# Revit family: Indirect-Water-Heater_AO_Smith-IT-500_G_B
name_source: partatom
category: Mechanical Equipment
revit_build: Autodesk Revit 2016 (Build: 20170117_1200(x64)
units: mm (PartAtom-declared; Revit-internal decimal feet)

## family parameters
Always vertical = Yes
Cut with Voids When Loaded = No
OmniClass Number = 23.75.00.00
OmniClass Title = Climate Control (HVAC)
Part Type = Normal
Room Calculation Point = No
Round Connector Dimension = Use Radius
Shared = No
Work Plane-Based = No

## types (1)
- Indirect-Water-Heater_AO_Smith-IT-500_G_B
    1e Maintenance (check-up) = 3 months after installation
    2nd Maintenance (general maintenance) = 12 months after installation
    Assembly Code = D3010
    BIM Content Developer = CAD & Company
    BIM Content Developer URL = http://www.cadcompany.nl
    Cold Water Connection R = 1 1/2"
    Description = Indirect Water Heater
    Destination / Counrty = UK & Ireland
    Diameter (with insulation) = 760 mm  [stored 2.49344 ft]
    Diameter (without insulation) = 600 mm  [stored 1.9685 ft]
    Draw-off Capacity @ ΔT = 28°C after 120 min. = 6935.0 L
    Draw-off Capacity @ ΔT = 28°C after 30 min. = 2328.0 L
    Draw-off Capacity @ ΔT = 28°C after 60 min. = 3864.0 L
    Draw-off Capacity @ ΔT = 28°C after 90 min. = 5400.0 L
    Draw-off Capacity @ ΔT = 44°C after 120 min. = 4413.0 L
    Draw-off Capacity @ ΔT = 44°C after 30 min. = 1482.0 L
    Draw-off Capacity @ ΔT = 44°C after 60 min. = 2459.0 L
    Draw-off Capacity @ ΔT = 44°C after 90 min. = 3436.0 L
    Draw-off Capacity @ ΔT = 50°C after 120 min. = 3884.0 L
    Draw-off Capacity @ ΔT = 50°C after 30 min. = 1304.0 L
    Draw-off Capacity @ ΔT = 50°C after 60 min. = 2164.0 L
    Draw-off Capacity @ ΔT = 50°C after 90 min. = 3024.0 L
    Draw-off Capacity @ ΔT = 55°C after 120 min. = 3531.0 L
    Draw-off Capacity @ ΔT = 55°C after 30 min. = 1185.0 L
    Draw-off Capacity @ ΔT = 55°C after 60 min. = 1967.0 L
    Draw-off Capacity @ ΔT = 55°C after 90 min. = 2749.0 L
    Draw-off Capacity @ ΔT = 70°C after 120 min. = 2774.0 L
    Draw-off Capacity @ ΔT = 70°C after 30 min. = 931.0 L
    Draw-off Capacity @ ΔT = 70°C after 60 min. = 1546.0 L
    Draw-off Capacity @ ΔT = 70°C after 90 min. = 2160.0 L
    Empty Weight = 180.00 kg
    Flow Rate - Volume L/h = 4300
    Heating Up Time @ ΔT = 28°C = 9
    Heating Up Time @ ΔT = 44°C = 15
    Heating Up Time @ ΔT = 50°C = 16
    Heating Up Time @ ΔT = 55°C = 18
    Heating Up Time @ ΔT = 70°C = 23
    Height (with insulation) = 2045 mm  [stored 6.70932 ft]
    Height (without insulation) = 1995 mm  [stored 6.54528 ft]
    Height Cold Water Inlet = 70 mm  [stored 0.229659 ft]
    Height Warm Water Outlet = 1995 mm  [stored 6.54528 ft]
    Hot / Warm Water Connection R = 1 1/2"
    Insulation Thickness = 80 mm  [stored 0.262467 ft]
    Maintenance Interval = 12 months
    Manufacturer = A.O. Smith Water Products Company b.v.
    Manufacturer Number = E 7110
E 7110
E 7110
    Max. Operating Pressure - bottom heat exchanger = 1600000.0 Pa
    Max. Operating Pressure - tank = 1000000.0 Pa
    Max. Tempature - bottom heat exchanger = 110 °C
    Max. Temperature - tank = 95 °C
    Model = IT 500 G B
    Nominal Output - bottom heat exchanger = 100000 W
    Operating Weight = 653.00 kg
    Packaging Height = 2150 mm
    Packaging Length = 780 mm  [stored 2.55906 ft]
    Packaging Width = 780 mm  [stored 2.55906 ft]
    Pressure Loss - bottom heat exchanger 80ºC/60ºC = 48900.0 Pa
    Product Documentation Link = https://www.aosmithinternational.com
    Product Instruction Link = https://www.aosmithinternational.com
    Recovery Rate @ ΔT = 28°C (ltr/hr) = 3071
    Recovery Rate @ ΔT = 44°C (ltr/hr) = 1955
    Recovery Rate @ ΔT = 50°C (ltr/hr) = 1720
    Recovery Rate @ ΔT = 55°C (ltr/hr) = 1564
    Recovery Rate @ ΔT = 70°C (ltr/hr) = 1229
    Serial Number = 8717449181505
    Stand-by Loss = 0 W
    Stand-by Loss - daily (Watt/24H) = 0
    Storage Capacity - bottom heat exchanger = 18.8 m³
    Storage Capacity - tank = 473 m³
    Surface bottom heat Exchanger = 3.11 m²
    T&P Connection Rp = 1"
    Transport Weight = 201.00 kg
    Type of Packaging = Plastic and Wood
    URL = www.aosmith.co.uk
    Warranty on Parts = 12 months
    Warranty on Tank = 36 months
    Workspace Diameter = 1760 mm  [stored 5.77428 ft]
    Workspace Height = 3045 mm

note: [stored X ft] marks values corroborated as IEEE doubles in the binary element streams (Revit-internal decimal feet)

## geometry (parser evidence)
native form markers: Blend x2, Sweep x25
no freeform markers — native parametric forms only
